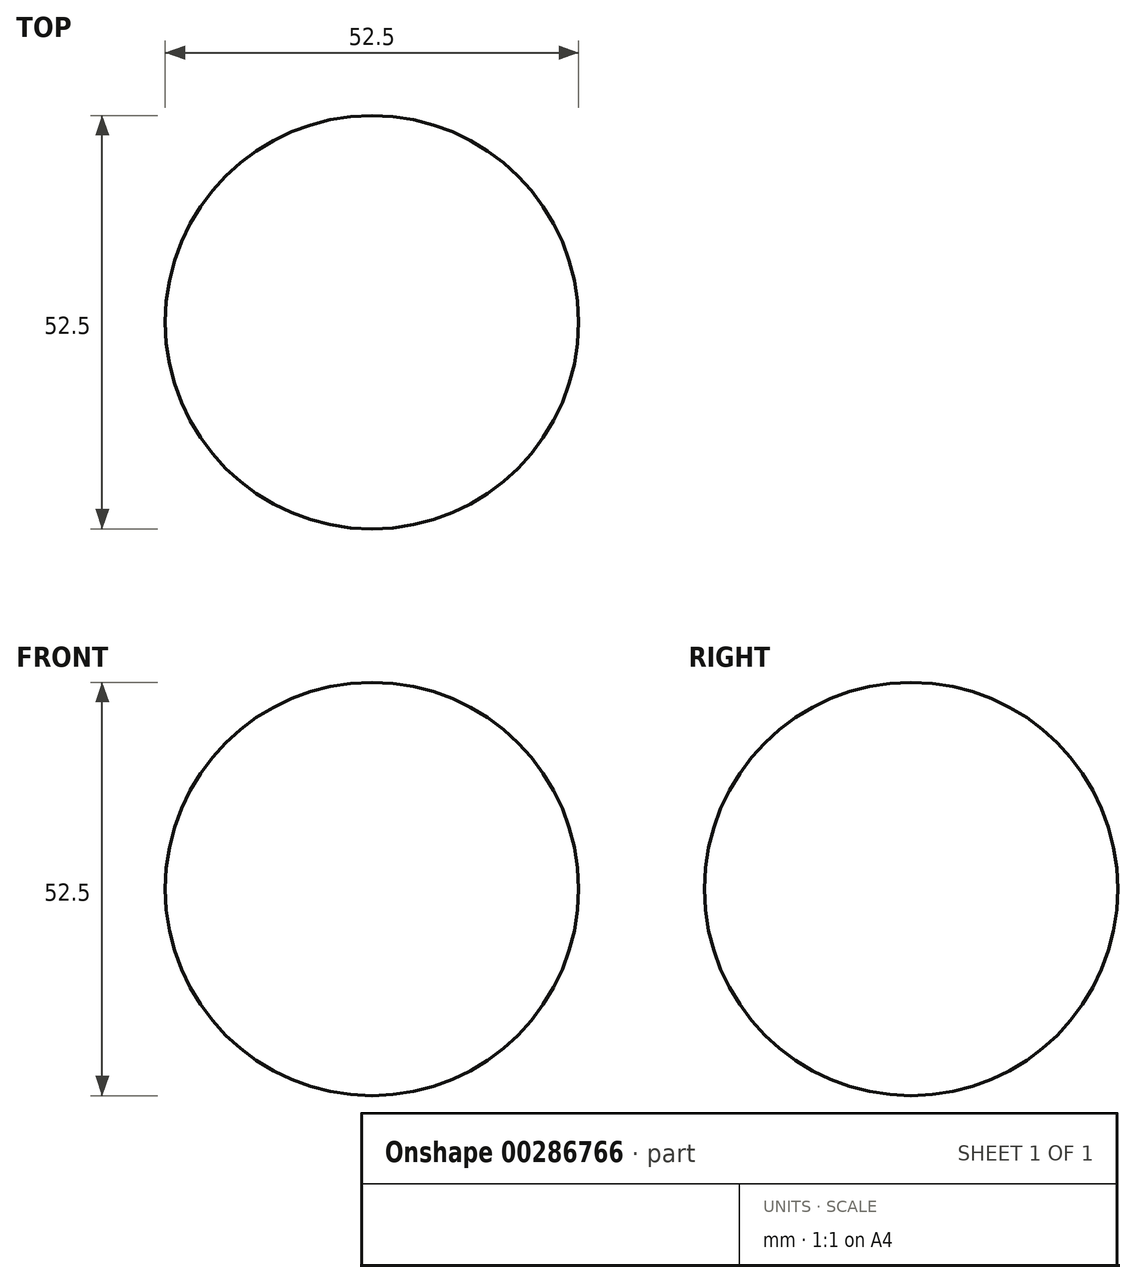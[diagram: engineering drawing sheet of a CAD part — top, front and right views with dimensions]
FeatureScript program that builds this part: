
annotation { "Feature Type Name" : "Feature", "Feature Type Description" : "" }
export const myFeature = defineFeature(function(context is Context, id is Id, definition is map)
    precondition{}
    {
        {
            var Q0;
            Q0=qCreatedBy(makeId("Top.planeOp"),FACE);
            var sketch = newSketch(context, id + "F0", { "sketchPlane" : qUnion([Q0])});
            skArc(sketch, "E0", {"start": v(0, 52.5) * mm, "mid": v(-26.25, 26.25) * mm, "end": v(0, 0) * mm});
            skPoint(sketch, "E1.orphan", {"position": v(0, 52.5) * mm});
            skPoint(sketch, "E2.start.orphan", {"position": v(0, 0) * mm});
            skLineSegment(sketch, "E3", {"start": v(0, 52.5) * mm, "end": v(0, 0) * mm});
            skSolve(sketch);
        }
        {
            var Q0;
            Q0=makeQuery(id+"F0.imprint","IMPRINT",FACE,{"disambiguationData":[TD([[makeQuery(id+"F0.imprint","IMPRINT",EDGE,{"derivedFrom":sQuery(id+"F0.wireOp",EDGE,"E0")}),1.0]])]});
            var Q1;
            Q1=sQuery(id+"F0.wireOp",EDGE,"E3");
            revolve(context, id + "F1", {"entities" : qUnion([Q0]), "axis" : qUnion([Q1]), "revolveType" : RevolveType.FULL});
        }
    });
